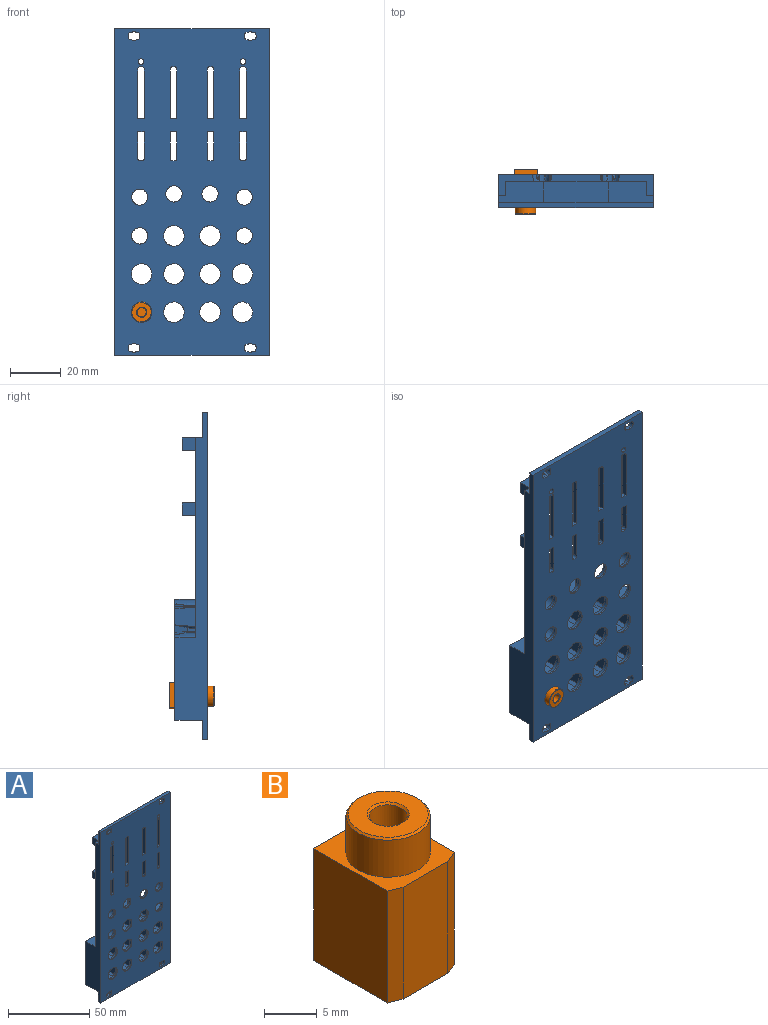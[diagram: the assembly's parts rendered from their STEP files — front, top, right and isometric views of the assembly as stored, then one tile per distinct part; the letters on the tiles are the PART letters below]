
ASSEMBLY  parts=2 mates=1
PART A: 342 faces, bbox 61x13.4x128.9 mm
  f0: plane 20.87x11.01mm, normal (0,0,1), area 212.7mm2, adj f2,f26,f41,f242,f243,f244,f251,f332
  f1: plane 11.04x7.93mm, normal (1,0,0), area 79.4mm2, adj f23,f26,f335,f336,f338,f339
  f2: plane 60.6x47.65mm, normal (0,1,0), area 1018.1mm2, adj f0,f3,f7,f58,f60,f151,f152,f193
  f3: plane 14.21x11.06mm, normal (0,0,1), area 143.7mm2, adj f2,f26,f60,f329,f330,f337,f341
  f4: plane 6.02x1.01mm, normal (-0.36,0,0.93), area 5.5mm2, adj f9,f26,f284,f337,f341
  f5: plane 8.98x6.03mm, normal (-1,0,0), area 51.9mm2, adj f8,f26,f335,f336,f338,f339
  f6: plane 8.73x6.03mm, normal (0,0,-1), area 51.2mm2, adj f7,f26,f281,f333,f340
  f7: plane 8.63x5.43mm, normal (0,0.14,-0.99), area 37.7mm2, adj f2,f6,f321,f340
  f8: plane 8.47x5.41mm, normal (-0.99,0.14,0), area 36.3mm2, adj f5,f23,f338,f339
  f9: plane 4.93x0.92mm, normal (-0.36,0.14,0.92), area 1.5mm2, adj f4,f323,f341
  f10: plane 11.52x2.8mm, normal (0,0,-1), area 32.3mm2, adj f26,f329,f330,f334
  f11: plane 12.62x2.8mm, normal (-1,0,0), area 35.3mm2, adj f26,f327,f330,f334
  f12: plane 55.02x10.1mm, normal (0,0,-1), area 441.7mm2, adj f13,f17,f24,f27,f42,f43,f80,f86
  f13: plane 20.52x5.24mm, normal (0,1,0), area 89.2mm2, adj f12,f15,f34,f80,f331
  f14: plane 55.02x10.1mm, normal (0,0,-1), area 456.1mm2, adj f25,f26,f41,f75,f79,f81,f85,f87
  f15: plane 55.02x10.1mm, normal (0,0,1), area 456.1mm2, adj f13,f17,f24,f25,f27,f33,f34,f35
  f16: plane 60.6x10mm, normal (0,1,0), area 579.8mm2, adj f44,f45,f46,f47,f48,f49,f50,f58
  f17: plane 20.52x7.11mm, normal (0,1,0), area 127.6mm2, adj f12,f15,f37,f114,f325
  f18: plane 60.6x7.5mm, normal (0,1,0), area 428.1mm2, adj f51,f52,f53,f54,f55,f56,f57,f58
  f19: plane 11x9.7mm, normal (0,1,0), area 40.2mm2, adj f140,f253,f254,f255,f256,f257,f258,f259
  f20: plane 11x9.7mm, normal (0,1,0), area 40.2mm2, adj f141,f260,f261,f262,f263,f264,f265,f266
  f21: plane 11x9.7mm, normal (0,1,0), area 40.2mm2, adj f136,f267,f268,f269,f270,f271,f272,f273
  f22: plane 11x9.7mm, normal (0,1,0), area 40.2mm2, adj f137,f274,f275,f276,f277,f278,f279,f280
  f23: plane 6.5x1.8mm, normal (0,1,0), area 11.1mm2, adj f1,f8,f338,f339
  f24: plane 20.52x5.24mm, normal (0,1,0), area 89.2mm2, adj f12,f15,f35,f113,f241
  f25: plane 5.3x5mm, normal (-1,0,0), area 26.5mm2, adj f14,f15,f134,f239
  f26: plane 49.28x25.8mm, normal (0,1,0), area 780.4mm2, adj f0,f1,f3,f4,f5,f6,f10,f11
  f27: plane 20.52x7.11mm, normal (0,1,0), area 127.6mm2, adj f12,f15,f40,f98,f232
  f28: plane 11.04x7.93mm, normal (-1,0,0), area 79.4mm2, adj f41,f192,f245,f247,f249,f250
  f29: plane 11x9.7mm, normal (0,1,0), area 40.2mm2, adj f144,f153,f154,f155,f156,f157,f158,f159
  f30: plane 11x9.7mm, normal (0,1,0), area 40.2mm2, adj f139,f160,f161,f162,f163,f164,f165,f166
  f31: plane 11x9.7mm, normal (0,1,0), area 40.2mm2, adj f135,f167,f168,f169,f170,f171,f172,f173
  f32: plane 11x9.7mm, normal (0,1,0), area 40.2mm2, adj f138,f174,f175,f176,f177,f178,f179,f180
  f33: plane 19.62x2mm, normal (-1,0,0), area 39.2mm2, adj f15,f43,f112,f126
  f34: plane 19.62x2mm, normal (1,0,0), area 39.2mm2, adj f13,f15,f80,f126
  f35: plane 19.62x2mm, normal (-1,0,0), area 39.2mm2, adj f15,f24,f113,f126
  f36: plane 19.62x2mm, normal (1,0,0), area 39.2mm2, adj f15,f42,f86,f126
  f37: plane 19.62x2mm, normal (-1,0,0), area 39.2mm2, adj f15,f17,f114,f126
  f38: plane 19.62x2mm, normal (1,0,0), area 39.2mm2, adj f15,f43,f92,f126
  f39: plane 19.62x2mm, normal (-1,0,0), area 39.2mm2, adj f15,f42,f115,f126
  f40: plane 19.62x2mm, normal (1,0,0), area 39.2mm2, adj f15,f27,f98,f126
  f41: plane 49.28x25.8mm, normal (0,1,0), area 780.4mm2, adj f0,f14,f28,f81,f82,f83,f84,f85
  f42: plane 20.52x12.05mm, normal (0,1,0), area 210.7mm2, adj f12,f15,f36,f39,f86,f115
  f43: plane 20.52x12.05mm, normal (0,1,0), area 210.7mm2, adj f12,f15,f33,f38,f92,f112
  f44: cylinder r=1.7mm len=2mm, axis (0,1,0), area 3.3mm2, adj f16,f45,f107,f126
  f45: plane 2x0.9mm, normal (0,0,-1), area 1.8mm2, adj f16,f44,f46,f126
  f46: cylinder r=2.17mm len=3mm, axis (0,1,0), area 6.6mm2, adj f16,f45,f47,f126
  f47: plane 2x0.9mm, normal (0,0,1), area 1.8mm2, adj f16,f46,f48,f126
  f48: cylinder r=1.7mm len=2mm, axis (0,1,0), area 3.3mm2, adj f16,f47,f49,f126
  f49: plane 2x0.9mm, normal (0,0,1), area 1.8mm2, adj f16,f48,f50,f126
  f50: cylinder r=2.17mm len=3mm, axis (0,1,0), area 6.6mm2, adj f16,f49,f107,f126
  f51: plane 2x0.9mm, normal (0,0,1), area 1.8mm2, adj f18,f52,f108,f126
  f52: cylinder r=2.17mm len=3mm, axis (0,1,0), area 6.6mm2, adj f18,f51,f53,f126
  f53: plane 2x0.9mm, normal (0,0,-1), area 1.8mm2, adj f18,f52,f54,f126
  f54: cylinder r=1.7mm len=2mm, axis (0,1,0), area 3.3mm2, adj f18,f53,f55,f126
  f55: plane 2x0.9mm, normal (0,0,-1), area 1.8mm2, adj f18,f54,f56,f126
  f56: cylinder r=2.17mm len=3mm, axis (0,1,0), area 6.6mm2, adj f18,f55,f57,f126
  f57: plane 2x0.9mm, normal (0,0,1), area 1.8mm2, adj f18,f56,f108,f126
  f58: plane 128.5x13mm, normal (-1,0,0), area 834.2mm2, adj f2,f16,f18,f59,f109,f126,f128,f151
  f59: plane 60.6x2mm, normal (0,0,-1), area 121.2mm2, adj f18,f58,f60,f126
  f60: plane 128.5x13mm, normal (1,0,0), area 834.2mm2, adj f2,f3,f16,f18,f59,f109,f126,f130
  f61: plane 2x0.9mm, normal (0,0,1), area 1.8mm2, adj f18,f62,f110,f126
  f62: cylinder r=2.17mm len=3mm, axis (0,1,0), area 6.6mm2, adj f18,f61,f63,f126
  f63: plane 2x0.9mm, normal (0,0,-1), area 1.8mm2, adj f18,f62,f64,f126
  f64: cylinder r=1.7mm len=2mm, axis (0,1,0), area 3.3mm2, adj f18,f63,f65,f126
  f65: plane 2x0.9mm, normal (0,0,-1), area 1.8mm2, adj f18,f64,f66,f126
  f66: cylinder r=2.17mm len=3mm, axis (0,1,0), area 6.6mm2, adj f18,f65,f67,f126
  f67: plane 2x0.9mm, normal (0,0,1), area 1.8mm2, adj f18,f66,f110,f126
  f68: plane 2x0.9mm, normal (0,0,1), area 1.8mm2, adj f16,f69,f111,f126
  f69: cylinder r=2.17mm len=3mm, axis (0,1,0), area 6.6mm2, adj f16,f68,f70,f126
  f70: plane 2x0.9mm, normal (0,0,-1), area 1.8mm2, adj f16,f69,f71,f126
  f71: cylinder r=1.7mm len=2mm, axis (0,1,0), area 3.3mm2, adj f16,f70,f72,f126
  f72: plane 2x0.9mm, normal (0,0,-1), area 1.8mm2, adj f16,f71,f73,f126
  f73: cylinder r=2.17mm len=3mm, axis (0,1,0), area 6.6mm2, adj f16,f72,f74,f126
  f74: plane 2x0.9mm, normal (0,0,1), area 1.8mm2, adj f16,f73,f111,f126
  f75: plane 10.58x2mm, normal (-1,0,0), area 21.2mm2, adj f14,f26,f76,f126
  f76: cylinder r=0.9mm len=2mm, axis (0,1,0), area 2.8mm2, adj f26,f75,f77,f126
  f77: plane 2x0.7mm, normal (0,0,1), area 1.4mm2, adj f26,f76,f78,f126
  f78: cylinder r=0.9mm len=2mm, axis (0,1,0), area 2.8mm2, adj f26,f77,f79,f126
  f79: plane 10.58x2mm, normal (1,0,0), area 21.2mm2, adj f14,f26,f78,f126
  f80: cylinder r=0.9mm len=2mm, axis (0,1,0), area 2.8mm2, adj f12,f13,f34,f126
  f81: plane 10.58x2mm, normal (-1,0,0), area 21.2mm2, adj f14,f41,f82,f126
  f82: cylinder r=0.9mm len=2mm, axis (0,1,0), area 2.8mm2, adj f41,f81,f83,f126
  f83: plane 2x0.7mm, normal (0,0,1), area 1.4mm2, adj f41,f82,f84,f126
  f84: cylinder r=0.9mm len=2mm, axis (0,1,0), area 2.8mm2, adj f41,f83,f85,f126
  f85: plane 10.58x2mm, normal (1,0,0), area 21.2mm2, adj f14,f41,f84,f126
  f86: cylinder r=0.9mm len=2mm, axis (0,1,0), area 2.8mm2, adj f12,f36,f42,f126
  f87: plane 10.58x2mm, normal (-1,0,0), area 21.2mm2, adj f14,f26,f88,f126
  f88: cylinder r=0.9mm len=2mm, axis (0,1,0), area 2.8mm2, adj f26,f87,f89,f126
  f89: plane 2x0.7mm, normal (0,0,1), area 1.4mm2, adj f26,f88,f90,f126
  f90: cylinder r=0.9mm len=2mm, axis (0,1,0), area 2.8mm2, adj f26,f89,f91,f126
  f91: plane 10.58x2mm, normal (1,0,0), area 21.2mm2, adj f14,f26,f90,f126
  f92: cylinder r=0.9mm len=2mm, axis (0,1,0), area 2.8mm2, adj f12,f38,f43,f126
  f93: plane 10.58x2mm, normal (-1,0,0), area 21.2mm2, adj f14,f41,f94,f126
  f94: cylinder r=0.9mm len=2mm, axis (0,1,0), area 2.8mm2, adj f41,f93,f95,f126
  f95: plane 2x0.7mm, normal (0,0,1), area 1.4mm2, adj f41,f94,f96,f126
  f96: cylinder r=0.9mm len=2mm, axis (0,1,0), area 2.8mm2, adj f41,f95,f97,f126
  f97: plane 10.58x2mm, normal (1,0,0), area 21.2mm2, adj f14,f41,f96,f126
  f98: cylinder r=0.9mm len=2mm, axis (0,1,0), area 2.8mm2, adj f12,f27,f40,f126
  f99: cylinder r=4.05mm len=8.1mm, axis (0,1,0), area 15.3mm2, adj f126,f135
  f100: cylinder r=4.05mm len=8.1mm, axis (0,1,0), area 15.3mm2, adj f126,f139
  f101: cylinder r=4.05mm len=8.1mm, axis (0,1,0), area 15.3mm2, adj f126,f137
  f102: cylinder r=4.05mm len=8.1mm, axis (0,1,0), area 15.3mm2, adj f126,f140
  f103: cylinder r=4.05mm len=8.1mm, axis (0,1,0), area 15.3mm2, adj f126,f143
  f104: cylinder r=3.2mm len=6.4mm, axis (0,1,0), area 12.1mm2, adj f126,f142
  f105: cylinder r=3.2mm len=6.4mm, axis (0,1,0), area 12.1mm2, adj f126,f149
  f106: cylinder r=3.15mm len=6.3mm, axis (0,1,0), area 11.9mm2, adj f126,f150
  f107: plane 2x0.9mm, normal (0,0,-1), area 1.8mm2, adj f16,f44,f50,f126
  f108: cylinder r=1.7mm len=2mm, axis (0,1,0), area 3.3mm2, adj f18,f51,f57,f126
  f109: plane 60.6x2mm, normal (0,0,1), area 121.2mm2, adj f16,f58,f60,f126
  f110: cylinder r=1.7mm len=2mm, axis (0,1,0), area 3.3mm2, adj f18,f61,f67,f126
  f111: cylinder r=1.7mm len=2mm, axis (0,1,0), area 3.3mm2, adj f16,f68,f74,f126
  f112: cylinder r=0.9mm len=2mm, axis (0,1,0), area 2.8mm2, adj f12,f33,f43,f126
  f113: cylinder r=0.9mm len=2mm, axis (0,1,0), area 2.8mm2, adj f12,f24,f35,f126
  f114: cylinder r=0.9mm len=2mm, axis (0,1,0), area 2.8mm2, adj f12,f17,f37,f126
  f115: cylinder r=0.9mm len=2mm, axis (0,1,0), area 2.8mm2, adj f12,f39,f42,f126
  f116: cylinder r=3.15mm len=6.3mm, axis (0,1,0), area 11.9mm2, adj f126,f147
  f117: cylinder r=1.1mm len=10.1mm, axis (0,1,0), area 69.8mm2, adj f126,f132
  f118: cylinder r=3.2mm len=6.4mm, axis (0,1,0), area 12.1mm2, adj f126,f148
  f119: cylinder r=3.2mm len=6.4mm, axis (0,1,0), area 12.1mm2, adj f126,f146
  f120: cylinder r=4.05mm len=8.1mm, axis (0,1,0), area 15.3mm2, adj f126,f141
  f121: cylinder r=4.05mm len=8.1mm, axis (0,1,0), area 15.3mm2, adj f126,f136
  f122: cylinder r=4.05mm len=8.1mm, axis (0,1,0), area 15.3mm2, adj f126,f145
  f123: cylinder r=4.05mm len=8.1mm, axis (0,1,0), area 15.3mm2, adj f126,f144
  f124: cylinder r=4.05mm len=8.1mm, axis (0,1,0), area 15.3mm2, adj f126,f138
  f125: cylinder r=1.1mm len=10.1mm, axis (0,1,0), area 69.8mm2, adj f126,f132
  f126: plane 128.5x60.6mm, normal (0,-1,0), area 6703.5mm2, adj f12,f14,f15,f33,f34,f35,f36,f37
  f127: plane 5.3x5mm, normal (-1,0,0), area 26.5mm2, adj f12,f128,f132,f239
  f128: plane 17.71x8.1mm, normal (0,0,1), area 128.7mm2, adj f16,f58,f127,f129,f132,f239
  f129: plane 25.18x8.1mm, normal (0,0,1), area 203.9mm2, adj f16,f128,f130,f132
  f130: plane 17.71x8.1mm, normal (0,0,1), area 128.7mm2, adj f16,f60,f129,f131,f132,f330
  f131: plane 5.3x5mm, normal (1,0,0), area 26.5mm2, adj f12,f130,f132,f330
  f132: plane 55.02x5mm, normal (0,1,0), area 267.5mm2, adj f12,f117,f125,f127,f128,f129,f130,f131
  f133: plane 5.3x5mm, normal (1,0,0), area 26.5mm2, adj f14,f15,f134,f330
  f134: plane 55.02x5mm, normal (0,1,0), area 275.1mm2, adj f14,f15,f25,f133
  f135: cone r=4.05mm half-angle=12deg, axis (0,1,0), area 37.8mm2, adj f31,f99
  f136: cone r=4.05mm half-angle=12deg, axis (0,1,0), area 37.8mm2, adj f21,f121
  f137: cone r=4.05mm half-angle=12deg, axis (0,1,0), area 37.8mm2, adj f22,f101
  f138: cone r=4.05mm half-angle=12deg, axis (0,1,0), area 37.8mm2, adj f32,f124
  f139: cone r=4.05mm half-angle=12deg, axis (0,1,0), area 37.8mm2, adj f30,f100
  f140: cone r=4.05mm half-angle=12deg, axis (0,1,0), area 37.8mm2, adj f19,f102
  f141: cone r=4.05mm half-angle=12deg, axis (0,1,0), area 37.8mm2, adj f20,f120
  f142: cone r=3.2mm half-angle=12deg, axis (0,1,0), area 30.1mm2, adj f26,f104
  f143: cone r=4.05mm half-angle=12deg, axis (0,1,0), area 37.8mm2, adj f26,f103
  f144: cone r=4.05mm half-angle=12deg, axis (0,1,0), area 37.8mm2, adj f29,f123
  f145: cone r=4.05mm half-angle=12deg, axis (0,1,0), area 37.8mm2, adj f41,f122
  f146: cone r=3.2mm half-angle=12deg, axis (0,1,0), area 30.1mm2, adj f41,f119
  f147: cone r=3.15mm half-angle=12deg, axis (0,1,0), area 29.7mm2, adj f116,f237
  f148: cone r=3.2mm half-angle=12deg, axis (0,1,0), area 30.1mm2, adj f41,f118
  f149: cone r=3.2mm half-angle=12deg, axis (0,1,0), area 30.1mm2, adj f26,f105
  f150: cone r=3.15mm half-angle=12deg, axis (0,1,0), area 29.7mm2, adj f106,f328
  f151: plane 60.6x11mm, normal (0,0,-1), area 666.6mm2, adj f2,f18,f58,f60
  f152: plane 14.21x11.06mm, normal (0,0,1), area 143.7mm2, adj f2,f41,f58,f235,f239,f248,f252
  f153: cylinder r=0.2mm len=6mm, axis (0,-1,0), area 5.7mm2, adj f29,f154,f187,f221
  f154: plane 8.9x6mm, normal (0,0,-1), area 53.4mm2, adj f29,f153,f155,f223
  f155: cylinder r=0.2mm len=6mm, axis (0,-1,0), area 5.7mm2, adj f29,f154,f156,f224
  f156: plane 9.97x6mm, normal (1,0,0), area 59.8mm2, adj f29,f155,f157,f222
  f157: plane 6x1.64mm, normal (0.36,0,0.93), area 10.6mm2, adj f29,f156,f158,f220
  f158: plane 6.01x6mm, normal (0,0,1), area 36.1mm2, adj f29,f157,f159,f218
  f159: plane 6x1.64mm, normal (-0.36,0,0.93), area 10.6mm2, adj f29,f158,f187,f217
  f160: cylinder r=0.2mm len=6mm, axis (0,-1,0), area 5.7mm2, adj f30,f161,f188,f212
  f161: plane 8.9x6mm, normal (0,0,-1), area 53.4mm2, adj f30,f160,f162,f210
  f162: cylinder r=0.2mm len=6mm, axis (0,-1,0), area 5.7mm2, adj f30,f161,f163,f209
  f163: plane 9.97x6mm, normal (1,0,0), area 59.8mm2, adj f30,f162,f164,f211
  f164: plane 6x1.64mm, normal (0.36,0,0.93), area 10.6mm2, adj f30,f163,f165,f213
  f165: plane 6.01x6mm, normal (0,0,1), area 36.1mm2, adj f30,f164,f166,f215
  f166: plane 6x1.64mm, normal (-0.36,0,0.93), area 10.6mm2, adj f30,f165,f188,f216
  f167: plane 6.01x6mm, normal (0,0,1), area 36.1mm2, adj f31,f168,f189,f194
  f168: plane 6x1.64mm, normal (-0.36,0,0.93), area 10.6mm2, adj f31,f167,f169,f193
  f169: plane 9.97x6mm, normal (-1,0,0), area 59.8mm2, adj f31,f168,f170,f195
  f170: cylinder r=0.2mm len=6mm, axis (0,-1,0), area 5.7mm2, adj f31,f169,f171,f197
  f171: plane 8.9x6mm, normal (0,0,-1), area 53.4mm2, adj f31,f170,f172,f199
  f172: cylinder r=0.2mm len=6mm, axis (0,-1,0), area 5.7mm2, adj f31,f171,f173,f200
  f173: plane 9.97x6mm, normal (1,0,0), area 59.8mm2, adj f31,f172,f189,f198
  f174: cylinder r=0.2mm len=6mm, axis (0,-1,0), area 5.7mm2, adj f32,f175,f190,f204
  f175: plane 8.9x6mm, normal (0,0,-1), area 53.4mm2, adj f32,f174,f176,f202
  f176: cylinder r=0.2mm len=6mm, axis (0,-1,0), area 5.7mm2, adj f32,f175,f177,f201
  f177: plane 9.97x6mm, normal (1,0,0), area 59.8mm2, adj f32,f176,f178,f203
  f178: plane 6x1.64mm, normal (0.36,0,0.93), area 10.6mm2, adj f32,f177,f179,f205
  f179: plane 6.01x6mm, normal (0,0,1), area 36.1mm2, adj f32,f178,f180,f207
  f180: plane 6x1.64mm, normal (-0.36,0,0.93), area 10.6mm2, adj f32,f179,f190,f208
  f181: cylinder r=0.2mm len=6mm, axis (0,-1,0), area 5.7mm2, adj f41,f182,f191,f227
  f182: plane 8.73x6.03mm, normal (0,0,-1), area 51.2mm2, adj f41,f181,f225,f244,f251
  f183: plane 8.98x6.03mm, normal (1,0,0), area 51.9mm2, adj f41,f226,f245,f247,f249,f250
  f184: plane 6.02x1.01mm, normal (0.36,0,0.93), area 5.5mm2, adj f41,f185,f228,f248,f252
  f185: plane 6.01x6mm, normal (0,0,1), area 36.1mm2, adj f41,f184,f186,f230
  f186: plane 6x1.64mm, normal (-0.36,0,0.93), area 10.6mm2, adj f41,f185,f191,f231
  f187: plane 9.97x6mm, normal (-1,0,0), area 59.8mm2, adj f29,f153,f159,f219
  f188: plane 9.97x6mm, normal (-1,0,0), area 59.8mm2, adj f30,f160,f166,f214
  f189: plane 6x1.64mm, normal (0.36,0,0.93), area 10.6mm2, adj f31,f167,f173,f196
  f190: plane 9.97x6mm, normal (-1,0,0), area 59.8mm2, adj f32,f174,f180,f206
  f191: plane 9.97x6mm, normal (-1,0,0), area 59.8mm2, adj f41,f181,f186,f229
  f192: plane 6.5x1.8mm, normal (0,1,0), area 11.1mm2, adj f28,f226,f249,f250
  f193: plane 5x2.35mm, normal (-0.36,0.14,0.92), area 10.4mm2, adj f2,f168,f194,f195
  f194: plane 6.27x5mm, normal (0,0.14,0.99), area 31mm2, adj f2,f167,f193,f196
  f195: plane 10.72x5.27mm, normal (-0.99,0.14,0), area 50.5mm2, adj f2,f169,f193,f197
  f196: plane 5x2.35mm, normal (0.36,0.14,0.92), area 10.4mm2, adj f2,f189,f194,f198
  f197: cone r=0.2mm half-angle=8deg, axis (0,1,0), area 10.1mm2, adj f2,f170,f195,f199
  f198: plane 10.72x5.27mm, normal (0.99,0.14,0), area 50.5mm2, adj f2,f173,f196,f200
  f199: plane 9.17x5.27mm, normal (0,0.14,-0.99), area 42.8mm2, adj f2,f171,f197,f200
  f200: cone r=0.2mm half-angle=8deg, axis (0,1,0), area 10.1mm2, adj f2,f172,f198,f199
  f201: cone r=0.2mm half-angle=8deg, axis (0,1,0), area 10.1mm2, adj f2,f176,f202,f203
  f202: plane 9.17x5.27mm, normal (0,0.14,-0.99), area 42.8mm2, adj f2,f175,f201,f204
  f203: plane 10.72x5.27mm, normal (0.99,0.14,0), area 50.5mm2, adj f2,f177,f201,f205
  f204: cone r=0.2mm half-angle=8deg, axis (0,1,0), area 10.1mm2, adj f2,f174,f202,f206
  f205: plane 5x2.35mm, normal (0.36,0.14,0.92), area 10.4mm2, adj f2,f178,f203,f207
  f206: plane 10.72x5.27mm, normal (-0.99,0.14,0), area 50.5mm2, adj f2,f190,f204,f208
  f207: plane 6.27x5mm, normal (0,0.14,0.99), area 31mm2, adj f2,f179,f205,f208
  f208: plane 5x2.35mm, normal (-0.36,0.14,0.92), area 10.4mm2, adj f2,f180,f206,f207
  f209: cone r=0.2mm half-angle=8deg, axis (0,1,0), area 10.1mm2, adj f2,f162,f210,f211
  f210: plane 9.17x5.27mm, normal (0,0.14,-0.99), area 42.8mm2, adj f2,f161,f209,f212
  f211: plane 10.72x5.27mm, normal (0.99,0.14,0), area 50.5mm2, adj f2,f163,f209,f213
  f212: cone r=0.2mm half-angle=8deg, axis (0,1,0), area 7.4mm2, adj f2,f160,f210,f214,f252
  f213: plane 5x2.35mm, normal (0.36,0.14,0.92), area 10.4mm2, adj f2,f164,f211,f215
  f214: plane 10.45x5mm, normal (-0.99,0.14,0), area 50.5mm2, adj f2,f188,f212,f216
  f215: plane 6.27x5mm, normal (0,0.14,0.99), area 31mm2, adj f2,f165,f213,f216
  f216: plane 5x2.35mm, normal (-0.36,0.14,0.92), area 10.4mm2, adj f2,f166,f214,f215
  f217: plane 5x2.35mm, normal (-0.36,0.14,0.92), area 10.4mm2, adj f2,f159,f218,f219
  f218: plane 6.27x5mm, normal (0,0.14,0.99), area 31mm2, adj f2,f158,f217,f220
  f219: plane 10.72x5.27mm, normal (-0.99,0.14,0), area 50.5mm2, adj f2,f187,f217,f221
  f220: plane 5x2.35mm, normal (0.36,0.14,0.92), area 10.4mm2, adj f2,f157,f218,f222
  f221: cone r=0.2mm half-angle=8deg, axis (0,1,0), area 10.1mm2, adj f2,f153,f219,f223
  f222: plane 10.72x5.27mm, normal (0.99,0.14,0), area 50.5mm2, adj f2,f156,f220,f224
  f223: plane 9.17x5.27mm, normal (0,0.14,-0.99), area 42.8mm2, adj f2,f154,f221,f224
  f224: cone r=0.2mm half-angle=8deg, axis (0,1,0), area 9.8mm2, adj f2,f155,f222,f223,f252
  f225: plane 8.63x5.43mm, normal (0,0.14,-0.99), area 37.7mm2, adj f2,f182,f227,f251
  f226: plane 8.47x5.41mm, normal (0.99,0.14,0), area 36.3mm2, adj f183,f192,f249,f250
  f227: cone r=0.2mm half-angle=8deg, axis (0,1,0), area 10.1mm2, adj f2,f181,f225,f229
  f228: plane 4.93x0.92mm, normal (0.36,0.14,0.92), area 1.5mm2, adj f184,f230,f252
  f229: plane 10.72x5.27mm, normal (-0.99,0.14,0), area 50.5mm2, adj f2,f191,f227,f231
  f230: plane 6.27x5mm, normal (0,0.14,0.99), area 31mm2, adj f2,f185,f228,f231,f252
  f231: plane 5x2.35mm, normal (-0.36,0.14,0.92), area 10.4mm2, adj f2,f186,f229,f230
  f232: plane 20.52x2.8mm, normal (1,0,0), area 57.5mm2, adj f12,f15,f27,f239
  f233: plane 18.02x2.8mm, normal (1,0,0), area 50.5mm2, adj f14,f41,f236,f239
  f234: plane 11.52x2.8mm, normal (0,0,-1), area 32.3mm2, adj f41,f235,f239,f246
  f235: plane 14.56x2.8mm, normal (1,0,0), area 40.8mm2, adj f41,f152,f234,f239
  f236: plane 13.26x2.8mm, normal (0,0,1), area 37.1mm2, adj f41,f233,f238,f239
  f237: cylinder r=3.45mm len=6.9mm, axis (0,-1,0), area 60.7mm2, adj f147,f239
  f238: plane 12.62x2.8mm, normal (1,0,0), area 35.3mm2, adj f41,f236,f239,f246
  f239: plane 78.52x16.05mm, normal (0,1,0), area 382.5mm2, adj f25,f58,f127,f128,f152,f232,f233,f234
  f240: plane 20.52x3.42mm, normal (0,1,0), area 70.2mm2, adj f12,f15,f241,f331
  f241: plane 20.52x2.8mm, normal (-1,0,0), area 57.5mm2, adj f12,f15,f24,f240
  f242: plane 32.83x2.8mm, normal (-1,0,0), area 91.9mm2, adj f0,f14,f41,f243
  f243: plane 32.83x3.42mm, normal (0,1,0), area 112.3mm2, adj f0,f14,f242,f332
  f244: cylinder r=2.8mm len=2.5mm, axis (0,1,0), area 5.6mm2, adj f0,f41,f182,f251
  f245: cylinder r=2.8mm len=2.5mm, axis (0,1,0), area 5.2mm2, adj f28,f41,f183,f250
  f246: cylinder r=2.8mm len=2.81mm, axis (0,1,0), area 9.9mm2, adj f41,f234,f238,f239
  f247: cylinder r=2.8mm len=2.5mm, axis (0,1,0), area 5.5mm2, adj f28,f41,f183,f249
  f248: cylinder r=2.8mm len=5.15mm, axis (0,1,0), area 15.9mm2, adj f41,f152,f184,f252
  f249: cone r=2.8mm half-angle=5deg, axis (0,1,0), area 22.4mm2, adj f28,f183,f192,f226,f247
  f250: cone r=2.8mm half-angle=5deg, axis (0,1,0), area 21.6mm2, adj f28,f183,f192,f226,f245
  f251: cone r=2.8mm half-angle=5deg, axis (0,1,0), area 22.6mm2, adj f0,f2,f182,f225,f244
  f252: cone r=2.8mm half-angle=5deg, axis (0,1,0), area 77.3mm2, adj f2,f152,f184,f212,f224,f228,f230,f248
  f253: cylinder r=0.2mm len=6mm, axis (0,-1,0), area 5.7mm2, adj f19,f254,f285,f317
  f254: plane 9.97x6mm, normal (1,0,0), area 59.8mm2, adj f19,f253,f255,f315
  f255: plane 6x1.64mm, normal (0.36,0,0.93), area 10.6mm2, adj f19,f254,f256,f313
  f256: plane 6.01x6mm, normal (0,0,1), area 36.1mm2, adj f19,f255,f257,f314
  f257: plane 6x1.64mm, normal (-0.36,0,0.93), area 10.6mm2, adj f19,f256,f258,f316
  f258: plane 9.97x6mm, normal (-1,0,0), area 59.8mm2, adj f19,f257,f259,f318
  f259: cylinder r=0.2mm len=6mm, axis (0,-1,0), area 5.7mm2, adj f19,f258,f285,f320
  f260: cylinder r=0.2mm len=6mm, axis (0,-1,0), area 5.7mm2, adj f20,f261,f286,f308
  f261: plane 9.97x6mm, normal (1,0,0), area 59.8mm2, adj f20,f260,f262,f310
  f262: plane 6x1.64mm, normal (0.36,0,0.93), area 10.6mm2, adj f20,f261,f263,f312
  f263: plane 6.01x6mm, normal (0,0,1), area 36.1mm2, adj f20,f262,f264,f311
  f264: plane 6x1.64mm, normal (-0.36,0,0.93), area 10.6mm2, adj f20,f263,f265,f309
  f265: plane 9.97x6mm, normal (-1,0,0), area 59.8mm2, adj f20,f264,f266,f307
  f266: cylinder r=0.2mm len=6mm, axis (0,-1,0), area 5.7mm2, adj f20,f265,f286,f305
  f267: plane 6.01x6mm, normal (0,0,1), area 36.1mm2, adj f21,f268,f287,f290
  f268: plane 6x1.64mm, normal (-0.36,0,0.93), area 10.6mm2, adj f21,f267,f269,f292
  f269: plane 9.97x6mm, normal (-1,0,0), area 59.8mm2, adj f21,f268,f270,f294
  f270: cylinder r=0.2mm len=6mm, axis (0,-1,0), area 5.7mm2, adj f21,f269,f271,f296
  f271: plane 8.9x6mm, normal (0,0,-1), area 53.4mm2, adj f21,f270,f272,f295
  f272: cylinder r=0.2mm len=6mm, axis (0,-1,0), area 5.7mm2, adj f21,f271,f273,f293
  f273: plane 9.97x6mm, normal (1,0,0), area 59.8mm2, adj f21,f272,f287,f291
  f274: cylinder r=0.2mm len=6mm, axis (0,-1,0), area 5.7mm2, adj f22,f275,f288,f300
  f275: plane 9.97x6mm, normal (1,0,0), area 59.8mm2, adj f22,f274,f276,f302
  f276: plane 6x1.64mm, normal (0.36,0,0.93), area 10.6mm2, adj f22,f275,f277,f304
  f277: plane 6.01x6mm, normal (0,0,1), area 36.1mm2, adj f22,f276,f278,f303
  f278: plane 6x1.64mm, normal (-0.36,0,0.93), area 10.6mm2, adj f22,f277,f279,f301
  f279: plane 9.97x6mm, normal (-1,0,0), area 59.8mm2, adj f22,f278,f280,f299
  f280: cylinder r=0.2mm len=6mm, axis (0,-1,0), area 5.7mm2, adj f22,f279,f288,f297
  f281: cylinder r=0.2mm len=6mm, axis (0,-1,0), area 5.7mm2, adj f6,f26,f282,f321
  f282: plane 9.97x6mm, normal (1,0,0), area 59.8mm2, adj f26,f281,f283,f322
  f283: plane 6x1.64mm, normal (0.36,0,0.93), area 10.6mm2, adj f26,f282,f284,f324
  f284: plane 6.01x6mm, normal (0,0,1), area 36.1mm2, adj f4,f26,f283,f323
  f285: plane 8.9x6mm, normal (0,0,-1), area 53.4mm2, adj f19,f253,f259,f319
  f286: plane 8.9x6mm, normal (0,0,-1), area 53.4mm2, adj f20,f260,f266,f306
  f287: plane 6x1.64mm, normal (0.36,0,0.93), area 10.6mm2, adj f21,f267,f273,f289
  f288: plane 8.9x6mm, normal (0,0,-1), area 53.4mm2, adj f22,f274,f280,f298
  f289: plane 5x2.35mm, normal (0.36,0.14,0.92), area 10.4mm2, adj f2,f287,f290,f291
  f290: plane 6.27x5mm, normal (0,0.14,0.99), area 31mm2, adj f2,f267,f289,f292
  f291: plane 10.72x5.27mm, normal (0.99,0.14,0), area 50.5mm2, adj f2,f273,f289,f293
  f292: plane 5x2.35mm, normal (-0.36,0.14,0.92), area 10.4mm2, adj f2,f268,f290,f294
  f293: cone r=0.9mm half-angle=8deg, axis (0,1,0), area 10.1mm2, adj f2,f272,f291,f295
  f294: plane 10.72x5.27mm, normal (-0.99,0.14,0), area 50.5mm2, adj f2,f269,f292,f296
  f295: plane 9.17x5.27mm, normal (0,0.14,-0.99), area 42.8mm2, adj f2,f271,f293,f296
  f296: cone r=0.9mm half-angle=8deg, axis (0,1,0), area 10.1mm2, adj f2,f270,f294,f295
  f297: cone r=0.9mm half-angle=8deg, axis (0,1,0), area 10.1mm2, adj f2,f280,f298,f299
  f298: plane 9.17x5.27mm, normal (0,0.14,-0.99), area 42.8mm2, adj f2,f288,f297,f300
  f299: plane 10.72x5.27mm, normal (-0.99,0.14,0), area 50.5mm2, adj f2,f279,f297,f301
  f300: cone r=0.9mm half-angle=8deg, axis (0,1,0), area 10.1mm2, adj f2,f274,f298,f302
  f301: plane 5x2.35mm, normal (-0.36,0.14,0.92), area 10.4mm2, adj f2,f278,f299,f303
  f302: plane 10.72x5.27mm, normal (0.99,0.14,0), area 50.5mm2, adj f2,f275,f300,f304
  f303: plane 6.27x5mm, normal (0,0.14,0.99), area 31mm2, adj f2,f277,f301,f304
  f304: plane 5x2.35mm, normal (0.36,0.14,0.92), area 10.4mm2, adj f2,f276,f302,f303
  f305: cone r=0.9mm half-angle=8deg, axis (0,1,0), area 10.1mm2, adj f2,f266,f306,f307
  f306: plane 9.17x5.27mm, normal (0,0.14,-0.99), area 42.8mm2, adj f2,f286,f305,f308
  f307: plane 10.72x5.27mm, normal (-0.99,0.14,0), area 50.5mm2, adj f2,f265,f305,f309
  f308: cone r=0.9mm half-angle=8deg, axis (0,1,0), area 7.4mm2, adj f2,f260,f306,f310,f341
  f309: plane 5x2.35mm, normal (-0.36,0.14,0.92), area 10.4mm2, adj f2,f264,f307,f311
  f310: plane 10.45x5mm, normal (0.99,0.14,0), area 50.5mm2, adj f2,f261,f308,f312
  f311: plane 6.27x5mm, normal (0,0.14,0.99), area 31mm2, adj f2,f263,f309,f312
  f312: plane 5x2.35mm, normal (0.36,0.14,0.92), area 10.4mm2, adj f2,f262,f310,f311
  f313: plane 5x2.35mm, normal (0.36,0.14,0.92), area 10.4mm2, adj f2,f255,f314,f315
  f314: plane 6.27x5mm, normal (0,0.14,0.99), area 31mm2, adj f2,f256,f313,f316
  f315: plane 10.72x5.27mm, normal (0.99,0.14,0), area 50.5mm2, adj f2,f254,f313,f317
  f316: plane 5x2.35mm, normal (-0.36,0.14,0.92), area 10.4mm2, adj f2,f257,f314,f318
  f317: cone r=0.9mm half-angle=8deg, axis (0,1,0), area 10.1mm2, adj f2,f253,f315,f319
  f318: plane 10.72x5.27mm, normal (-0.99,0.14,0), area 50.5mm2, adj f2,f258,f316,f320
  f319: plane 9.17x5.27mm, normal (0,0.14,-0.99), area 42.8mm2, adj f2,f285,f317,f320
  f320: cone r=0.9mm half-angle=8deg, axis (0,1,0), area 9.8mm2, adj f2,f259,f318,f319,f341
  f321: cone r=0.9mm half-angle=8deg, axis (0,1,0), area 10.1mm2, adj f2,f7,f281,f322
  f322: plane 10.72x5.27mm, normal (0.99,0.14,0), area 50.5mm2, adj f2,f282,f321,f324
  f323: plane 6.27x5mm, normal (0,0.14,0.99), area 31mm2, adj f2,f9,f284,f324,f341
  f324: plane 5x2.35mm, normal (0.36,0.14,0.92), area 10.4mm2, adj f2,f283,f322,f323
  f325: plane 20.52x2.8mm, normal (-1,0,0), area 57.5mm2, adj f12,f15,f17,f330
  f326: plane 18.02x2.8mm, normal (-1,0,0), area 50.5mm2, adj f14,f26,f327,f330
  f327: plane 13.26x2.8mm, normal (0,0,1), area 37.1mm2, adj f11,f26,f326,f330
  f328: cylinder r=3.45mm len=6.9mm, axis (0,-1,0), area 60.7mm2, adj f150,f330
  f329: plane 14.56x2.8mm, normal (-1,0,0), area 40.8mm2, adj f3,f10,f26,f330
  f330: plane 78.52x16.05mm, normal (0,1,0), area 382.5mm2, adj f3,f10,f11,f60,f130,f131,f133,f325
  f331: plane 20.52x2.8mm, normal (1,0,0), area 57.5mm2, adj f12,f13,f15,f240
  f332: plane 32.83x2.8mm, normal (1,0,0), area 91.9mm2, adj f0,f14,f26,f243
  f333: cylinder r=2.8mm len=2.5mm, axis (0,1,0), area 5.6mm2, adj f0,f6,f26,f340
  f334: cylinder r=2.8mm len=2.81mm, axis (0,1,0), area 9.9mm2, adj f10,f11,f26,f330
  f335: cylinder r=2.8mm len=2.5mm, axis (0,1,0), area 5.2mm2, adj f1,f5,f26,f339
  f336: cylinder r=2.8mm len=2.5mm, axis (0,1,0), area 5.5mm2, adj f1,f5,f26,f338
  f337: cylinder r=2.8mm len=5.15mm, axis (0,1,0), area 15.9mm2, adj f3,f4,f26,f341
  f338: cone r=3.59mm half-angle=5deg, axis (0,1,0), area 22.4mm2, adj f1,f5,f8,f23,f336
  f339: cone r=3.59mm half-angle=5deg, axis (0,1,0), area 21.6mm2, adj f1,f5,f8,f23,f335
  f340: cone r=3.59mm half-angle=5deg, axis (0,1,0), area 22.6mm2, adj f0,f2,f6,f7,f333
  f341: cone r=3.59mm half-angle=5deg, axis (0,1,0), area 77.3mm2, adj f2,f3,f4,f9,f308,f320,f323,f337
PART B: 14 faces, bbox 9x10.5x17.5 mm
  f0: plane 13x1.5mm, normal (0.37,-0.93,0), area 21mm2, adj f1,f5,f6,f7
  f1: plane 13x9.9mm, normal (1,0,0), area 128.7mm2, adj f0,f2,f6,f7
  f2: plane 13x9mm, normal (0,1,0), area 117mm2, adj f1,f3,f6,f7
  f3: plane 13x9.9mm, normal (-1,0,0), area 128.7mm2, adj f2,f4,f6,f7
  f4: plane 13x1.5mm, normal (-0.37,-0.93,0), area 21mm2, adj f3,f5,f6,f7
  f5: plane 13x6mm, normal (0,-1,0), area 78mm2, adj f0,f4,f6,f7
  f6: plane 10.5x9mm, normal (0,0,1), area 43.3mm2, adj f0,f1,f2,f3,f4,f5,f9
  f7: plane 10.5x9mm, normal (0,0,-1), area 93.6mm2, adj f0,f1,f2,f3,f4,f5
  f8: cylinder r=1.8mm len=4.3mm, axis (0,0,-1), area 48.6mm2, adj f11,f12
  f9: cylinder r=4mm len=8mm, axis (0,0,-1), area 108.1mm2, adj f6,f13
  f10: plane 7.6x7.6mm, normal (0,0,1), area 32.8mm2, adj f12,f13
  f11: plane 3.6x3.6mm, normal (0,0,1), area 10.2mm2, adj f8
  f12: cone r=1.8mm half-angle=45deg, axis (0,0,1), area 3.4mm2, adj f8,f10
  f13: cone r=3.8mm half-angle=45deg, axis (0,0,-1), area 6.9mm2, adj f9,f10
PLACE A at identity fixed
PLACE B rot(axis=(1,0,0),90deg) t=(-19.8,13,-47.25)mm
MATE slider B.f8 <-> A.f99  axis (0,-1,0) through (-19.8,0,-47.25)mm
